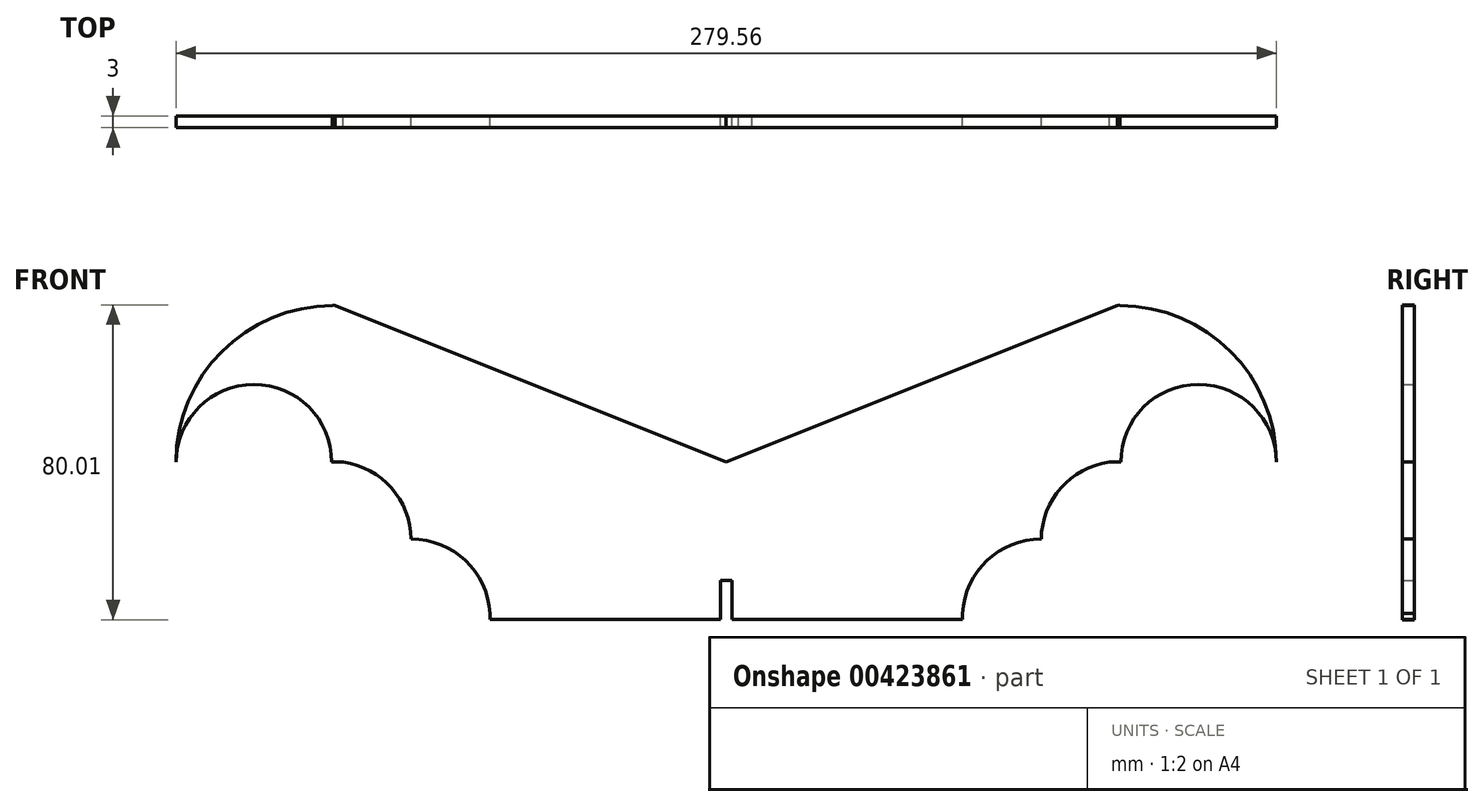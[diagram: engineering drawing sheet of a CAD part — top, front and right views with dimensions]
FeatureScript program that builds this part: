
annotation { "Feature Type Name" : "Feature", "Feature Type Description" : "" }
export const myFeature = defineFeature(function(context is Context, id is Id, definition is map)
    precondition{}
    {
        {
            var Q0;
            Q0=qCreatedBy(makeId("Front.planeOp"),FACE);
            var sketch = newSketch(context, id + "F0", { "sketchPlane" : qUnion([Q0])});
            skLineSegment(sketch, "E0.bottom", {"start": v(-63.07, 21.49) * mm, "end": v(56.93, 21.49) * mm});
            skLineSegment(sketch, "E0.top", {"start": v(-63.07, -18.51) * mm, "end": v(-4.52, -18.51) * mm});
            skLineSegment(sketch, "E0.left", {"start": v(-63.07, 21.49) * mm, "end": v(-63.07, -18.51) * mm});
            skLineSegment(sketch, "E0.right", {"start": v(56.93, -16.93) * mm, "end": v(56.93, -18.51) * mm});
            skLineSegment(sketch, "E1.bottom", {"start": v(-63.07, 21.49) * mm, "end": v(-63.3, 21.49) * mm});
            skLineSegment(sketch, "E1.left", {"start": v(-63.07, 21.49) * mm, "end": v(-63.07, -18.09) * mm});
            skPoint(sketch, "E2", {"position": v(-83.07, -18.09) * mm});
            skPoint(sketch, "E3", {"position": v(-83.07, 21.49) * mm});
            skArc(sketch, "E4", {"start": v(-63.04, -18.51) * mm, "mid": v(-68.77, -4.06) * mm, "end": v(-83.1, 1.95) * mm});
            skPoint(sketch, "E5", {"position": v(-103.07, 1.7) * mm});
            skLineSegment(sketch, "E6", {"start": v(-103.07, 21.49) * mm, "end": v(-103.32, 21.49) * mm});
            skPoint(sketch, "E7", {"position": v(-123.07, 21.49) * mm});
            skArc(sketch, "E8", {"start": v(-103.32, 21.49) * mm, "mid": v(-123.07, 41.24) * mm, "end": v(-142.82, 21.49) * mm});
            skLineSegment(sketch, "E9", {"start": v(-103.07, 21.49) * mm, "end": v(-103.07, 21.67) * mm});
            skLineSegment(sketch, "E10", {"start": v(-103.07, 61.49) * mm, "end": v(-102.49, 61.26) * mm});
            skLineSegment(sketch, "E11.trimOffspring", {"start": v(-142.82, 21.49) * mm, "end": v(-143.07, 21.49) * mm});
            skArc(sketch, "E12.trimOffspring", {"start": v(-83.1, 1.95) * mm, "mid": v(-89.13, 16) * mm, "end": v(-103.32, 21.67) * mm});
            skPoint(sketch, "E1.right.end.orphan", {"position": v(-103.07, -18.09) * mm});
            skLineSegment(sketch, "E13.trimOffspring", {"start": v(-100.37, 21.49) * mm, "end": v(-103.07, 21.49) * mm});
            skLineSegment(sketch, "E14.trimOffspring", {"start": v(-103.07, 61.27) * mm, "end": v(-103.07, 61.49) * mm});
            skArc(sketch, "E15.trimOffspring", {"start": v(-102.49, 61.26) * mm, "mid": v(-130.99, 49.82) * mm, "end": v(-142.85, 21.49) * mm});
            skLineSegment(sketch, "E16", {"start": v(-63.07, 21.49) * mm, "end": v(-3.07, 21.49) * mm});
            skLineSegment(sketch, "E17", {"start": v(-102.49, 61.26) * mm, "end": v(-3.07, 21.49) * mm});
            skPoint(sketch, "E18.start.orphan", {"position": v(0, 21.49) * mm});
            skLineSegment(sketch, "E19", {"start": v(-3.07, 21.49) * mm, "end": v(-3.07, -8.51) * mm});
            skLineSegment(sketch, "E20.MirrorCS", {"start": v(96.93, 21.49) * mm, "end": v(97.18, 21.49) * mm});
            skLineSegment(sketch, "E21.MirrorCS", {"start": v(94.23, 21.49) * mm, "end": v(96.93, 21.49) * mm});
            skLineSegment(sketch, "E22.MirrorCS", {"start": v(96.93, 21.49) * mm, "end": v(96.93, 21.67) * mm});
            skLineSegment(sketch, "E23.MirrorCS", {"start": v(56.93, 21.49) * mm, "end": v(57.15, 21.49) * mm});
            skLineSegment(sketch, "E24.MirrorCS", {"start": v(96.93, 61.27) * mm, "end": v(96.93, 61.49) * mm});
            skLineSegment(sketch, "E25.MirrorCS", {"start": v(136.68, 21.49) * mm, "end": v(136.93, 21.49) * mm});
            skLineSegment(sketch, "E26.MirrorCS", {"start": v(96.93, 61.49) * mm, "end": v(96.35, 61.26) * mm});
            skLineSegment(sketch, "E27.MirrorCS", {"start": v(56.93, 21.49) * mm, "end": v(56.93, -18.51) * mm});
            skLineSegment(sketch, "E28.MirrorCS", {"start": v(96.35, 61.26) * mm, "end": v(-3.07, 21.49) * mm});
            skPoint(sketch, "E29.MirrorP", {"position": v(116.93, 21.49) * mm});
            skLineSegment(sketch, "E30.MirrorCS", {"start": v(56.93, 21.49) * mm, "end": v(-3.07, 21.49) * mm});
            skArc(sketch, "E31.MirrorCS", {"start": v(76.96, 1.95) * mm, "mid": v(82.99, 16) * mm, "end": v(97.18, 21.67) * mm});
            skArc(sketch, "E32.MirrorCS", {"start": v(96.35, 61.26) * mm, "mid": v(124.85, 49.82) * mm, "end": v(136.7, 21.49) * mm});
            skPoint(sketch, "E33.MirrorP", {"position": v(76.93, 21.49) * mm});
            skPoint(sketch, "E34.MirrorP", {"position": v(-6.14, 21.49) * mm});
            skPoint(sketch, "E35.MirrorP", {"position": v(76.93, -18.09) * mm});
            skPoint(sketch, "E36.MirrorP", {"position": v(96.93, -18.09) * mm});
            skArc(sketch, "E37.MirrorCS", {"start": v(97.18, 21.49) * mm, "mid": v(116.93, 41.24) * mm, "end": v(136.68, 21.49) * mm});
            skLineSegment(sketch, "E38.MirrorCS", {"start": v(56.93, -16.93) * mm, "end": v(56.93, -18.09) * mm});
            skArc(sketch, "E39.MirrorCS", {"start": v(56.9, -18.51) * mm, "mid": v(62.63, -4.06) * mm, "end": v(76.96, 1.95) * mm});
            skLineSegment(sketch, "E40.top", {"start": v(-4.52, -8.51) * mm, "end": v(-1.62, -8.51) * mm});
            skLineSegment(sketch, "E40.left", {"start": v(-4.52, -18.51) * mm, "end": v(-4.52, -8.51) * mm});
            skLineSegment(sketch, "E40.right", {"start": v(-1.62, -18.51) * mm, "end": v(-1.62, -8.51) * mm});
            skPoint(sketch, "E40.middle", {"position": v(-3.07, -18.51) * mm});
            skPoint(sketch, "E40.bottom.end.orphan", {"position": v(-1.62, -28.51) * mm});
            skPoint(sketch, "E40.bottom.start.orphan", {"position": v(-4.52, -28.51) * mm});
            skLineSegment(sketch, "E41.trimOffspring", {"start": v(-1.62, -18.51) * mm, "end": v(56.93, -18.51) * mm});
            skArc(sketch, "E42", {"start": v(-66.37, -7.02) * mm, "mid": v(-35.97, -15.61) * mm, "end": v(-4.52, -18.51) * mm});
            skArc(sketch, "E43", {"start": v(0, -18.51) * mm, "mid": v(30.11, -16.15) * mm, "end": v(59.33, -8.51) * mm});
            skSolve(sketch);
        }
        {
            var Q0;
            Q0 = qSketchRegion(id + "F0", true);
            extrude(context, id + "F1", {"entities" : qUnion([Q0]), "depth" : 3 * mm});
        }
        {
            var Q0;
            Q0 = qSketchRegion(id + "F0", true);
            extrude(context, id + "F2", {"entities" : qUnion([Q0]), "depth" : 3 * mm});
        }
        {
            var Q0;
            Q0 = qSketchRegion(id + "F0", true);
            extrude(context, id + "F3", {"entities" : qUnion([Q0]), "depth" : 3 * mm});
        }
    });
